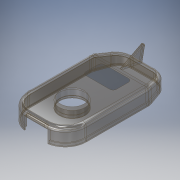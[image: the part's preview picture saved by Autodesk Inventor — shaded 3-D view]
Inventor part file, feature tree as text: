
AUTODESK INVENTOR PART (.ipt)
format: ipt  version: 2019 (Build 230136000, 136)  size: 434,176 bytes
history: native  units: mm
features: sketch x12, extrude x7, fillet x5, other x4, projected_geometry x4, plane x1, loft x1, shell x1, split x1, draft x1, sweep x1
ambient origin geometry x8: Origin, YZ Plane, XZ Plane, XY Plane, X Axis, Y Axis, Z Axis, Center Point
bodies: Body1 (feature_tree)
feature tree (38):
  other  "ROV Hull - Top Half"
  extrude  "Extrusion1"  Depth=360.0mm
  plane  "Work Plane1"
  loft  "Loft1"
  fillet  "Fillet1"  Radius=100.0mm
  fillet  "Fillet2"  Radius=180.0mm
  fillet  "Fillet3"  Radius=40.0mm
  shell  "Shell1"  Thickness=0.0mm
  other  "Lip1"
  extrude  "Extrusion2"  Depth=60.0mm
  extrude  "Extrusion3"  Depth=16.0mm
  other  "Lip3"
  split  "Split1"
  sketch  "Sketch6"  dims[d17=10.0mm d18=5.0mm d19=0.0mm d20=0.0mm d21=0.0mm d22=0.0mm d24=110.0mm d25=100.0mm d26=20.0mm d27=0.0mm]
  extrude  "Extrusion4"  Depth=100.0mm
  draft  "FaceDraft1"
  fillet  "Fillet4"  Radius=100.0mm
  fillet  "Fillet5"  Radius=20.0mm
  extrude  "Extrusion5"  Depth=10.0mm
  extrude  "Extrusion6"  Depth=70.0mm
  extrude  "Extrusion7"  Depth=3.0mm
  sweep  "Sweep1"
  sketch  "Sketch1"  dims[d0=250.0mm d1=360.0mm]
  sketch  "Sketch2"  dims[d2=90.0mm d3=60.0mm d4=0.0mm d5=100.0mm d7=180.0mm d8=40.0mm d9=0.0mm d10=90.0deg]
  other  "Edges1"
  sketch  "Sketch3"  dims[d11=0.0mm d12=90.0deg d13=60.0mm]
  projected_geometry  "Projected Loop2"
  sketch  "Sketch4"  dims[d14=50.0mm d15=16.0mm]
  projected_geometry  "Projected Loop3"
  sketch  "Sketch5"  dims[d16=10.0mm]
  sketch  "Sketch7"  dims[d34=15.0mm d35=0.0mm]
  sketch  "Sketch8"  dims[d36=10.0mm d37=2.5mm d38=0.0mm d39=0.0mm d40=0.0mm d41=0.0mm d44=15.0mm]
  sketch  "Sketch9"  dims[d45=70.0mm d46=0.0mm d47=6.719518mm]
  projected_geometry  "Projected Loop6"
  sketch  "Sketch10"  dims[d48=5.0mm d49=3.0mm]
  sketch  "Sketch11"  dims[d50=138.4mm d51=5.0mm]
  projected_geometry  "Projected Loop7"
  sketch  "Sketch12"  dims[d53=10.0mm d54=0.0mm d55=8.0mm d56=120.0mm d57=0.0mm d58=100.0mm d59=15.0mm d60=0.0mm d61=90.0mm d62=5.0mm d76=10.381932mm d77=0.0mm d78=0.0mm]
